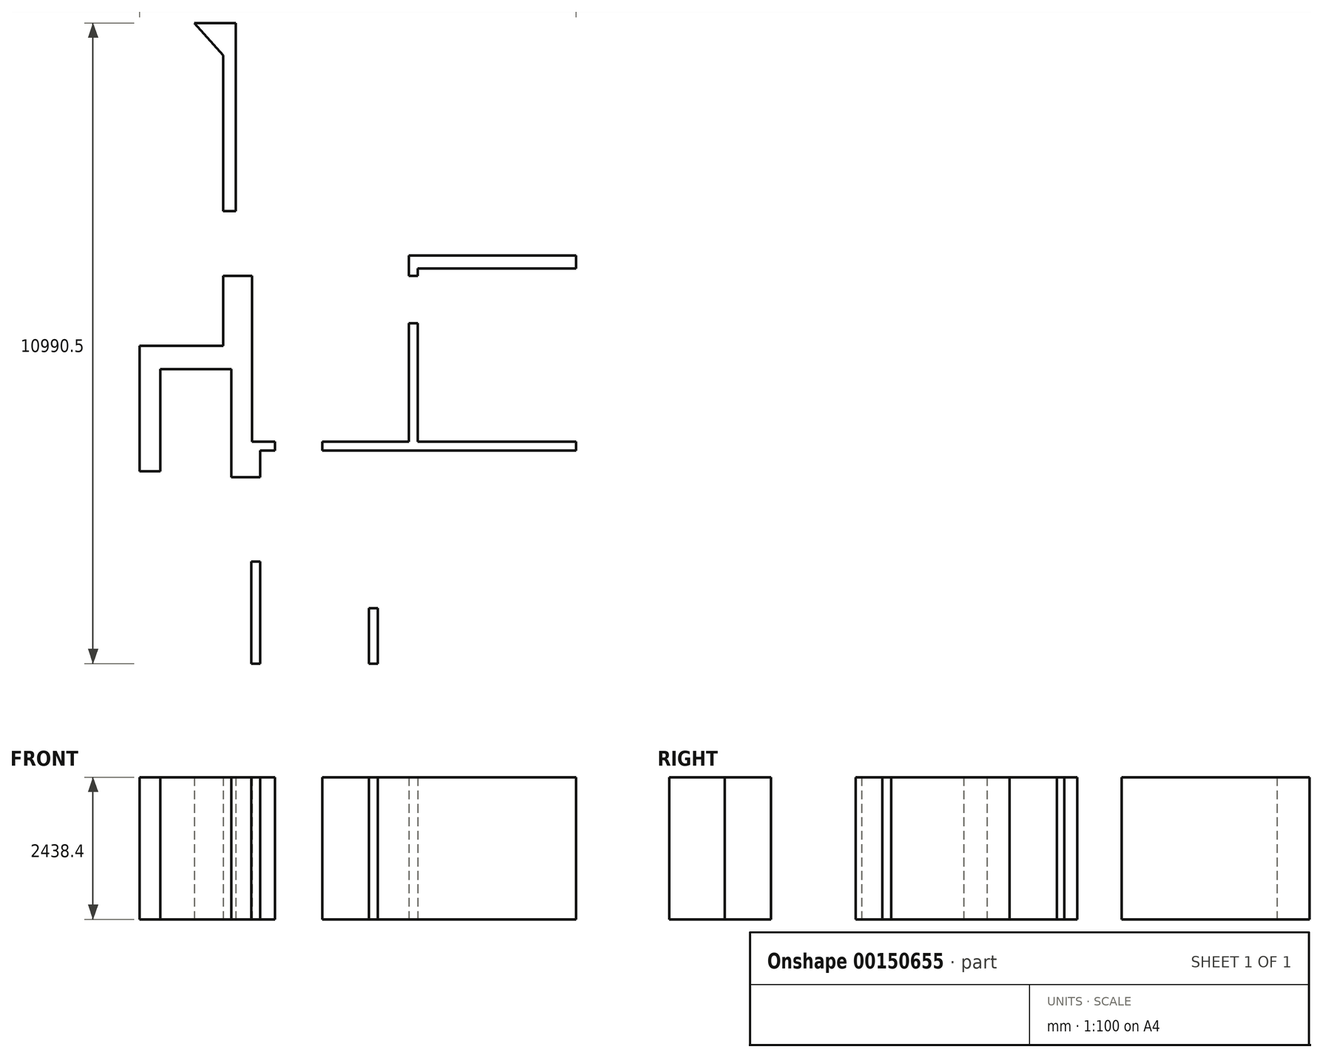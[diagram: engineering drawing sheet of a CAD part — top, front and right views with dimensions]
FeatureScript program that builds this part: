
annotation { "Feature Type Name" : "Feature", "Feature Type Description" : "" }
export const myFeature = defineFeature(function(context is Context, id is Id, definition is map)
    precondition{}
    {
        {
            var Q0;
            Q0=qCreatedBy(makeId("Top.planeOp"),FACE);
            var sketch = newSketch(context, id + "F0", { "sketchPlane" : qUnion([Q0])});
            skLineSegment(sketch, "E0.top", {"start": v(-1828.7, -2008.63) * mm, "end": v(1574.9, -2008.63) * mm});
            skLineSegment(sketch, "E0.left", {"start": v(-1828.7, -1058.26) * mm, "end": v(-1828.7, -2008.63) * mm});
            skLineSegment(sketch, "E0.right", {"start": v(1574.9, 1648.97) * mm, "end": v(1574.9, -2008.63) * mm});
            skLineSegment(sketch, "E1.top", {"start": v(-1981.1, -2008.63) * mm, "end": v(-3847.34, -2008.63) * mm});
            skLineSegment(sketch, "E1.left", {"start": v(-1981.1, -1058.26) * mm, "end": v(-1981.1, -2008.63) * mm});
            skLineSegment(sketch, "E1.right", {"start": v(-3847.34, 1648.97) * mm, "end": v(-3847.34, 1188.76) * mm});
            skLineSegment(sketch, "E2.bottom", {"start": v(-3999.74, -2008.63) * mm, "end": v(-9663.94, -2008.63) * mm});
            skLineSegment(sketch, "E2.left", {"start": v(-3999.74, -2008.63) * mm, "end": v(-3999.74, -261.74) * mm});
            skLineSegment(sketch, "E3.bottom", {"start": v(-1142.9, 1801.37) * mm, "end": v(1574.9, 1801.37) * mm});
            skLineSegment(sketch, "E3.top", {"start": v(-1142.9, 4773.17) * mm, "end": v(1574.9, 4773.17) * mm});
            skLineSegment(sketch, "E3.left", {"start": v(-1142.9, 1801.37) * mm, "end": v(-1142.9, 3833.37) * mm});
            skLineSegment(sketch, "E3.right", {"start": v(1574.9, 1801.37) * mm, "end": v(1574.9, 4773.17) * mm});
            skLineSegment(sketch, "E4.top", {"start": v(-3987.7, 1801.37) * mm, "end": v(-3594.17, 1801.37) * mm});
            skLineSegment(sketch, "E4.left", {"start": v(-3987.7, 4646.17) * mm, "end": v(-3987.7, 1801.37) * mm});
            skLineSegment(sketch, "E4.right", {"start": v(-1295.3, 3833.37) * mm, "end": v(-1295.3, 1801.37) * mm});
            skLineSegment(sketch, "E5.top", {"start": v(1574.9, 8981.86) * mm, "end": v(-4267.1, 8981.86) * mm});
            skLineSegment(sketch, "E5.left", {"start": v(1574.9, 4994.06) * mm, "end": v(1574.9, 8981.86) * mm});
            skLineSegment(sketch, "E6.top", {"start": v(-4343.3, 3045.97) * mm, "end": v(-5562.5, 3045.97) * mm});
            skLineSegment(sketch, "E6.left", {"start": v(-4343.3, 1191.77) * mm, "end": v(-4343.3, 3045.97) * mm});
            skLineSegment(sketch, "E6.right", {"start": v(-5562.5, 1293.37) * mm, "end": v(-5562.5, 3045.97) * mm});
            skLineSegment(sketch, "E7.trimOffspring", {"start": v(-5562.5, 1293.37) * mm, "end": v(-5918.1, 1293.37) * mm});
            skLineSegment(sketch, "E8.right", {"start": v(-5918.1, 1293.37) * mm, "end": v(-5918.1, 3045.97) * mm});
            skLineSegment(sketch, "E9", {"start": v(-9663.94, 3045.97) * mm, "end": v(-10012.83, 3394.85) * mm});
            skLineSegment(sketch, "E10", {"start": v(-10012.83, 3394.85) * mm, "end": v(-6366.6, 6633.55) * mm});
            skLineSegment(sketch, "E11", {"start": v(-6366.6, 6633.55) * mm, "end": v(-6920.8, 7257.48) * mm});
            skLineSegment(sketch, "E12", {"start": v(-6920.8, 7257.48) * mm, "end": v(-4979.44, 8981.86) * mm});
            skLineSegment(sketch, "E13", {"start": v(-4484.7, 8424.87) * mm, "end": v(-4484.7, 5930.26) * mm});
            skLineSegment(sketch, "E14", {"start": v(-4979.44, 8981.86) * mm, "end": v(-4484.7, 8424.87) * mm});
            skLineSegment(sketch, "E15", {"start": v(-9663.94, 3045.97) * mm, "end": v(-9663.94, -2008.63) * mm});
            skLineSegment(sketch, "E16", {"start": v(-5918.1, 3045.97) * mm, "end": v(-5918.1, 3442.42) * mm});
            skLineSegment(sketch, "E17", {"start": v(-1295.3, 4646.17) * mm, "end": v(-1142.9, 4646.17) * mm});
            skLineSegment(sketch, "E18", {"start": v(-1142.9, 3833.37) * mm, "end": v(-1295.3, 3833.37) * mm});
            skLineSegment(sketch, "E19.trimOffspring", {"start": v(-1142.9, 4646.17) * mm, "end": v(-1142.9, 4773.17) * mm});
            skLineSegment(sketch, "E20", {"start": v(-5918.1, 3442.42) * mm, "end": v(-4484.7, 3442.42) * mm});
            skLineSegment(sketch, "E21", {"start": v(-4267.1, 8981.86) * mm, "end": v(-4267.1, 5756.06) * mm});
            skLineSegment(sketch, "E22", {"start": v(-4267.1, 5756.06) * mm, "end": v(-4484.7, 5756.06) * mm});
            skLineSegment(sketch, "E23", {"start": v(-4484.7, 5756.06) * mm, "end": v(-4484.7, 5930.26) * mm});
            skLineSegment(sketch, "E24", {"start": v(-3594.17, 1801.37) * mm, "end": v(-3594.17, 1648.97) * mm});
            skLineSegment(sketch, "E25", {"start": v(-2781.37, 1648.97) * mm, "end": v(-2781.37, 1801.37) * mm});
            skLineSegment(sketch, "E26.trimOffspring", {"start": v(-2781.37, 1801.37) * mm, "end": v(-1295.3, 1801.37) * mm});
            skLineSegment(sketch, "E27.trimOffspring", {"start": v(-3594.17, 1648.97) * mm, "end": v(-3847.34, 1648.97) * mm});
            skLineSegment(sketch, "E28", {"start": v(-3999.74, -261.74) * mm, "end": v(-3847.34, -261.74) * mm});
            skLineSegment(sketch, "E29.trimOffspring", {"start": v(-3847.34, -261.74) * mm, "end": v(-3847.34, -2008.63) * mm});
            skLineSegment(sketch, "E30", {"start": v(-1981.1, -1058.26) * mm, "end": v(-1828.7, -1058.26) * mm});
            skLineSegment(sketch, "E31", {"start": v(-4484.7, 3442.42) * mm, "end": v(-4484.7, 4646.17) * mm});
            skLineSegment(sketch, "E32", {"start": v(-4484.7, 4646.17) * mm, "end": v(-3987.7, 4646.17) * mm});
            skLineSegment(sketch, "E33", {"start": v(-3999.74, -2008.63) * mm, "end": v(-3847.34, -2008.63) * mm});
            skLineSegment(sketch, "E34", {"start": v(-1981.1, -2008.63) * mm, "end": v(-1828.7, -2008.63) * mm});
            skLineSegment(sketch, "E35", {"start": v(1574.9, 1801.37) * mm, "end": v(1574.9, 1648.97) * mm});
            skLineSegment(sketch, "E36", {"start": v(-4979.44, 8981.86) * mm, "end": v(-4267.1, 8981.86) * mm});
            skLineSegment(sketch, "E37", {"start": v(1574.9, 4994.06) * mm, "end": v(1574.9, 4773.17) * mm});
            skLineSegment(sketch, "E38", {"start": v(-1295.3, 4646.17) * mm, "end": v(-1295.3, 4994.06) * mm});
            skLineSegment(sketch, "E39", {"start": v(-1295.3, 4994.06) * mm, "end": v(1574.9, 4994.06) * mm});
            skLineSegment(sketch, "E40", {"start": v(-2781.37, 1648.97) * mm, "end": v(1574.9, 1648.97) * mm});
            skLineSegment(sketch, "E41", {"start": v(-4343.3, 1191.77) * mm, "end": v(-3847.34, 1188.76) * mm});
            skSolve(sketch);
        }
        {
            var Q0;
            Q0 = qSketchRegion(id + "F0", true);
            var Q1;
            Q1=sQuery(id+"F0.wireOp",EDGE,"E15");
            var Q2;
            Q2=sQuery(id+"F0.wireOp",EDGE,"E9");
            var Q3;
            Q3=sQuery(id+"F0.wireOp",EDGE,"E10");
            var Q4;
            Q4=sQuery(id+"F0.wireOp",EDGE,"E11");
            var Q5;
            Q5=sQuery(id+"F0.wireOp",EDGE,"E12");
            var Q6;
            Q6=sQuery(id+"F0.wireOp",EDGE,"E5.top");
            var Q7;
            Q7=sQuery(id+"F0.wireOp",EDGE,"E36");
            var Q8;
            Q8=sQuery(id+"F0.wireOp",EDGE,"E5.left");
            var Q9;
            Q9=sQuery(id+"F0.wireOp",EDGE,"E37");
            var Q10;
            Q10=sQuery(id+"F0.wireOp",EDGE,"E3.right");
            var Q11;
            Q11=sQuery(id+"F0.wireOp",EDGE,"E0.right");
            var Q12;
            Q12=sQuery(id+"F0.wireOp",EDGE,"E0.top");
            var Q13;
            Q13=sQuery(id+"F0.wireOp",EDGE,"E34");
            var Q14;
            Q14=sQuery(id+"F0.wireOp",EDGE,"E1.top");
            var Q15;
            Q15=sQuery(id+"F0.wireOp",EDGE,"E33");
            var Q16;
            Q16=sQuery(id+"F0.wireOp",EDGE,"E2.bottom");
            var Q17;
            Q17=sQuery(id+"F0.wireOp",EDGE,"E35");
            extrude(context, id + "F1", {"entities" : qUnion([Q0]), "bodyType" : ToolBodyType.SURFACE, "surfaceEntities" : qUnion([Q1, Q2, Q3, Q4, Q5, Q6, Q7, Q8, Q9, Q10, Q11, Q12, Q13, Q14, Q15, Q16, Q17]), "depth" : 2438.4 * mm});
        }
        {
            var Q0;
            Q0=makeQuery(id+"F0.imprint","IMPRINT",FACE,{"disambiguationData":[TD([[makeQuery(id+"F0.imprint","IMPRINT",EDGE,{"derivedFrom":sQuery(id+"F0.wireOp",EDGE,"E1.right")}),-1.0]])]});
            var Q1;
            Q1=makeQuery(id+"F0.imprint","IMPRINT",FACE,{"disambiguationData":[TD([[makeQuery(id+"F0.imprint","IMPRINT",EDGE,{"derivedFrom":sQuery(id+"F0.wireOp",EDGE,"E13")}),1.0]])]});
            var Q2;
            Q2=makeQuery(id+"F0.imprint","IMPRINT",FACE,{"disambiguationData":[TD([[makeQuery(id+"F0.imprint","IMPRINT",EDGE,{"derivedFrom":sQuery(id+"F0.wireOp",EDGE,"E3.top")}),1.0]])]});
            var Q3;
            Q3=makeQuery(id+"F0.imprint","IMPRINT",FACE,{"disambiguationData":[TD([[makeQuery(id+"F0.imprint","IMPRINT",EDGE,{"derivedFrom":sQuery(id+"F0.wireOp",EDGE,"E3.bottom")}),-1.0]])]});
            var Q4;
            Q4=makeQuery(id+"F0.imprint","IMPRINT",FACE,{"disambiguationData":[TD([[makeQuery(id+"F0.imprint","IMPRINT",EDGE,{"derivedFrom":sQuery(id+"F0.wireOp",EDGE,"E2.left")}),-1.0]])]});
            var Q5;
            Q5=makeQuery(id+"F0.imprint","IMPRINT",FACE,{"disambiguationData":[TD([[makeQuery(id+"F0.imprint","IMPRINT",EDGE,{"derivedFrom":sQuery(id+"F0.wireOp",EDGE,"E0.left")}),-1.0]])]});
            extrude(context, id + "F2", {"entities" : qUnion([Q0, Q1, Q2, Q3, Q4, Q5]), "depth" : 2438.4 * mm});
        }
    });
